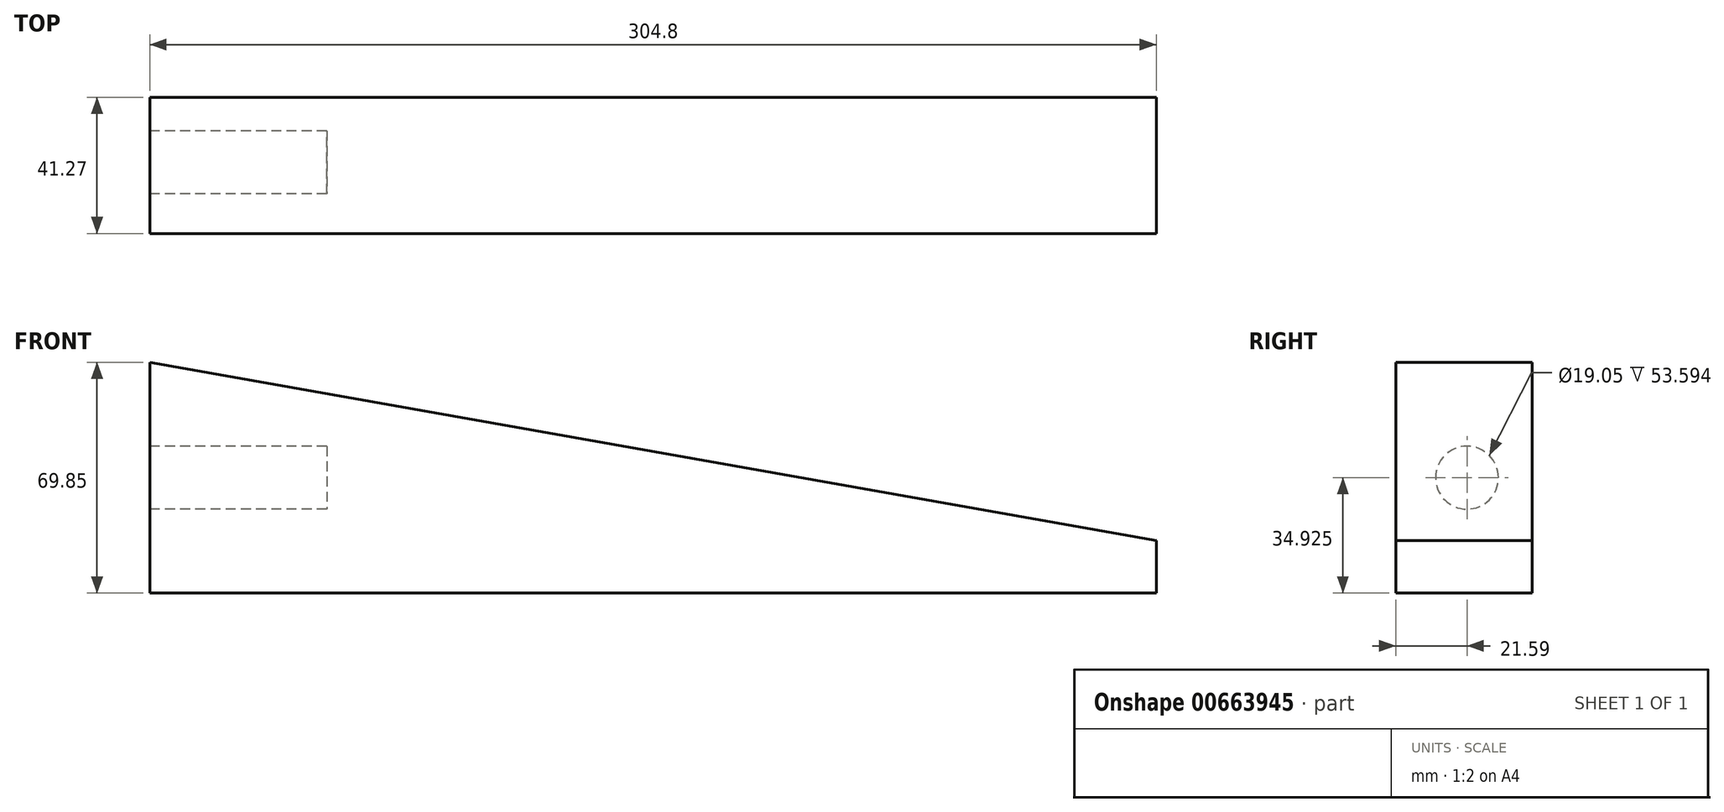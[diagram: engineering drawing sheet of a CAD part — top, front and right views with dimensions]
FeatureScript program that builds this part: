
annotation { "Feature Type Name" : "Feature", "Feature Type Description" : "" }
export const myFeature = defineFeature(function(context is Context, id is Id, definition is map)
    precondition{}
    {
        {
            var Q0;
            Q0=qCreatedBy(makeId("Front.planeOp"),FACE);
            var sketch = newSketch(context, id + "F0", { "sketchPlane" : qUnion([Q0])});
            skLineSegment(sketch, "E0", {"start": v(0, 0) * mm, "end": v(304.8, 0) * mm});
            skLineSegment(sketch, "E1", {"start": v(304.8, 0) * mm, "end": v(304.8, 15.88) * mm});
            skLineSegment(sketch, "E2", {"start": v(0, 0) * mm, "end": v(0, 69.85) * mm});
            skLineSegment(sketch, "E3", {"start": v(0, 69.85) * mm, "end": v(304.8, 15.88) * mm});
            skSolve(sketch);
        }
        {
            var Q0;
            Q0=makeQuery(id+"F0.imprint","IMPRINT",FACE,{"disambiguationData":[TD([[makeQuery(id+"F0.imprint","IMPRINT",EDGE,{"derivedFrom":sQuery(id+"F0.wireOp",EDGE,"E0")}),1.0]])]});
            extrude(context, id + "F1", {"entities" : qUnion([Q0]), "oppositeDirection" : true, "depth" : 41.27 * mm, "offsetDistance" : 25.4 * mm});
        }
        {
            var Q0;
            Q0=makeQuery(id+"F1.opExtrude","SWEPT_FACE",FACE,{"disambiguationData":[OSD([sQuery(id+"F0.wireOp",EDGE,"E2")])]});
            var sketch = newSketch(context, id + "F2", { "sketchPlane" : qUnion([Q0])});
            skLineSegment(sketch, "E4", {"start": v(0, 34.93) * mm, "end": v(-21.59, 34.93) * mm});
            skCircle(sketch, "E5", {"center": v(-21.59, 34.93) * mm, "radius": 9.53 * mm});
            skSolve(sketch);
        }
        {
            var Q0;
            Q0=makeQuery(id+"F2.imprint","IMPRINT",FACE,{"disambiguationData":[TD([[makeQuery(id+"F2.imprint","IMPRINT",EDGE,{"derivedFrom":sQuery(id+"F2.wireOp",EDGE,"E5")}),1.0]])]});
            extrude(context, id + "F3", {"entities" : qUnion([Q0]), "operationType" : NewBodyOperationType.REMOVE, "oppositeDirection" : true, "depth" : 53.6 * mm, "offsetDistance" : 25.4 * mm});
        }
    });
